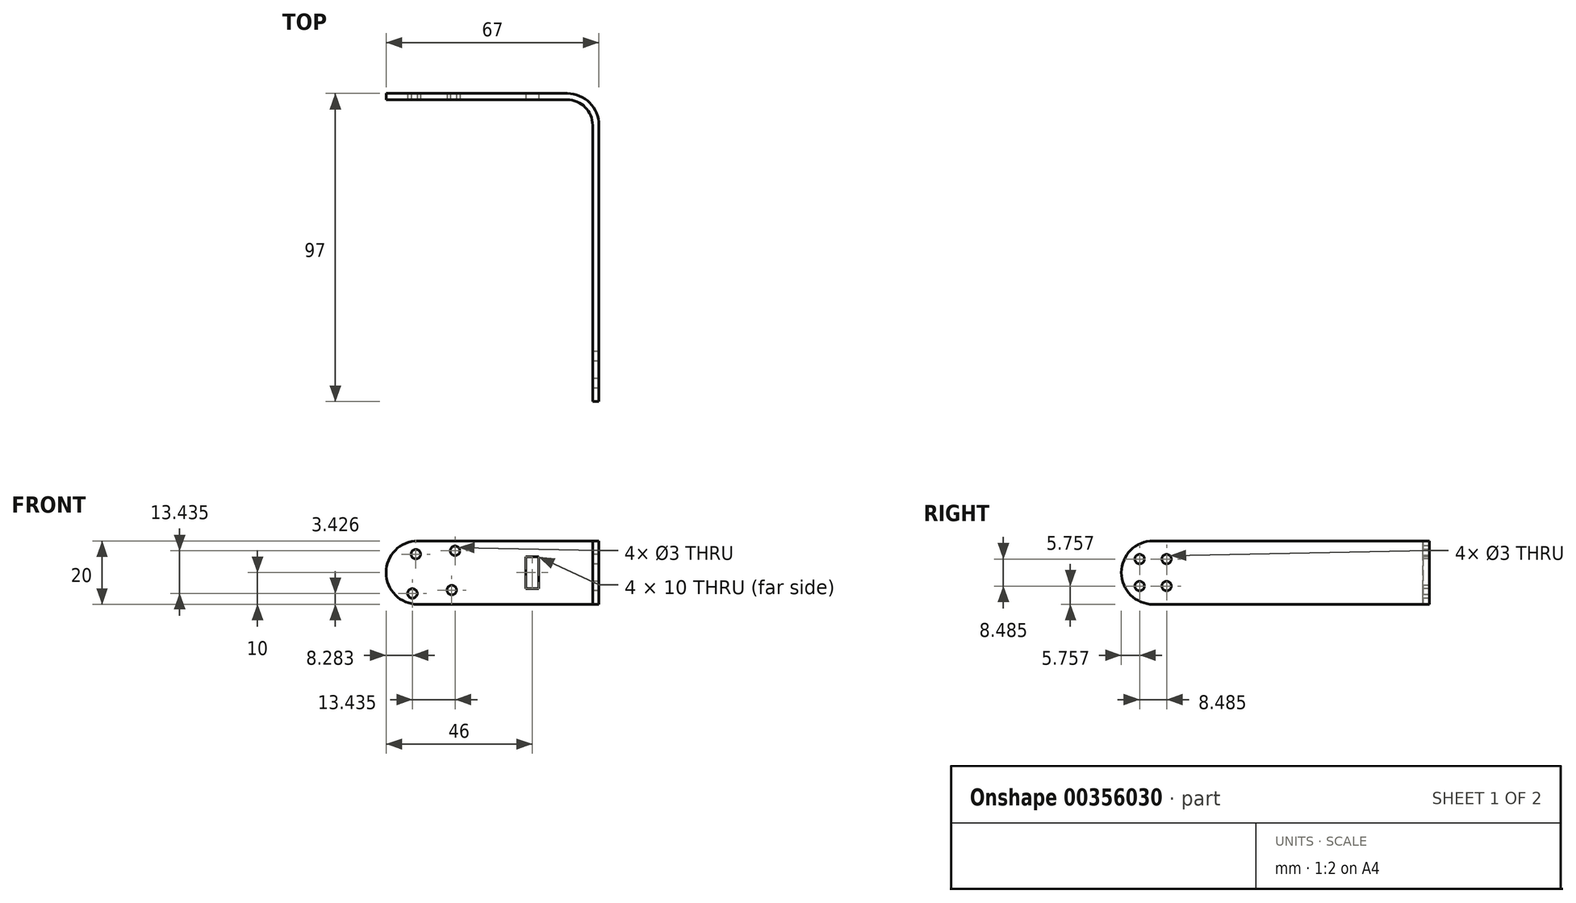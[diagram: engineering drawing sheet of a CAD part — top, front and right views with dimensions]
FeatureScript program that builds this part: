
annotation { "Feature Type Name" : "Feature", "Feature Type Description" : "" }
export const myFeature = defineFeature(function(context is Context, id is Id, definition is map)
    precondition{}
    {
        {
            var Q0;
            Q0=qCreatedBy(makeId("Top.planeOp"),FACE);
            var sketch = newSketch(context, id + "F0", { "sketchPlane" : qUnion([Q0])});
            skLineSegment(sketch, "E0", {"start": v(0, 0) * mm, "end": v(57, 0) * mm});
            skLineSegment(sketch, "E1", {"start": v(65, -8) * mm, "end": v(65, -95) * mm});
            skLineSegment(sketch, "E2.0", {"start": v(67, -8) * mm, "end": v(67, -95) * mm});
            skLineSegment(sketch, "E2.1", {"start": v(0, 2) * mm, "end": v(57, 2) * mm});
            skLineSegment(sketch, "E3", {"start": v(0, 2) * mm, "end": v(0, 0) * mm});
            skLineSegment(sketch, "E4", {"start": v(65, -95) * mm, "end": v(67, -95) * mm});
            skPoint(sketch, "E5.visualSharp", {"position": v(65, 0) * mm});
            skArc(sketch, "E5.filletArc", {"start": v(65, -8) * mm, "mid": v(62.66, -2.34) * mm, "end": v(57, 0) * mm});
            skPoint(sketch, "E6.visualSharp", {"position": v(67, 2) * mm});
            skArc(sketch, "E6.filletArc", {"start": v(67, -8) * mm, "mid": v(64.07, -0.93) * mm, "end": v(57, 2) * mm});
            skSolve(sketch);
        }
        {
            var Q0;
            Q0=qSketchRegion(id+"F0",true);
            extrude(context, id + "F1", {"entities" : qUnion([Q0]), "depth" : 20 * mm});
        }
        {
            var Q0;
            Q0=makeQuery(id+"F1.opExtrude","SWEPT_FACE",FACE,{"disambiguationData":[OSD([sQuery(id+"F0.wireOp",EDGE,"E0")])]});
            var sketch = newSketch(context, id + "F2", { "sketchPlane" : qUnion([Q0])});
            skLineSegment(sketch, "E7", {"start": v(15, 36.62) * mm, "end": v(15, -16.34) * mm});
            skPoint(sketch, "E8", {"position": v(15, 10.14) * mm});
            skLineSegment(sketch, "E9.bottom", {"start": v(44, 15) * mm, "end": v(48, 15) * mm});
            skLineSegment(sketch, "E9.top", {"start": v(44, 5) * mm, "end": v(48, 5) * mm});
            skLineSegment(sketch, "E9.left", {"start": v(44, 15) * mm, "end": v(44, 5) * mm});
            skLineSegment(sketch, "E9.right", {"start": v(48, 15) * mm, "end": v(48, 5) * mm});
            skPoint(sketch, "E10", {"position": v(44, 10) * mm});
            skPoint(sketch, "E11.3.0", {"position": v(21.72, 16.86) * mm});
            skPoint(sketch, "E11.7.0", {"position": v(8.28, 3.43) * mm});
            skPoint(sketch, "E12", {"position": v(15, 2.14) * mm});
            skPoint(sketch, "E13.1.0", {"position": v(20.66, 4.49) * mm});
            skPoint(sketch, "E13.5.0", {"position": v(9.34, 15.8) * mm});
            skSolve(sketch);
        }
        {
            var Q0;
            Q0=makeQuery(id+"F1.opExtrude","SWEPT_FACE",FACE,{"disambiguationData":[OSD([sQuery(id+"F0.wireOp",EDGE,"E1")])]});
            var sketch = newSketch(context, id + "F3", { "sketchPlane" : qUnion([Q0])});
            skLineSegment(sketch, "E14", {"start": v(75, 20) * mm, "end": v(75, 0) * mm, "construction": true});
            skLineSegment(sketch, "E15", {"start": v(75, 10) * mm, "end": v(95, 10) * mm, "construction": true});
            skLineSegment(sketch, "E16", {"start": v(85, 20) * mm, "end": v(85, 0) * mm, "construction": true});
            skPoint(sketch, "E16.startSnap0", {"position": v(85, 10) * mm});
            skPoint(sketch, "E17.middle", {"position": v(32.8, 10) * mm});
            skPoint(sketch, "E18.1.0", {"position": v(80.76, 14.24) * mm});
            skPoint(sketch, "E18.3.0", {"position": v(80.76, 5.76) * mm});
            skPoint(sketch, "E18.5.0", {"position": v(89.24, 5.76) * mm});
            skPoint(sketch, "E18.7.0", {"position": v(89.24, 14.24) * mm});
            skSolve(sketch);
        }
        {
            var Q0;
            Q0=makeQuery(id+"F1.opExtrude","CAP_EDGE",EDGE,{"disambiguationData":[OSD([sQuery(id+"F0.wireOp",EDGE,"E3")])],"isStart":false});
            var Q1;
            Q1=makeQuery(id+"F1.opExtrude","CAP_EDGE",EDGE,{"disambiguationData":[OSD([sQuery(id+"F0.wireOp",EDGE,"E3")])],"isStart":true});
            var Q2;
            Q2=makeQuery(id+"F1.opExtrude","CAP_EDGE",EDGE,{"disambiguationData":[OSD([sQuery(id+"F0.wireOp",EDGE,"E4")])],"isStart":false});
            var Q3;
            Q3=makeQuery(id+"F1.opExtrude","CAP_EDGE",EDGE,{"disambiguationData":[OSD([sQuery(id+"F0.wireOp",EDGE,"E4")])],"isStart":true});
            fillet(context, id + "F4", {"entities" : qUnion([Q0, Q1, Q2, Q3]), "radius" : 10 * mm, "tangentPropagation" : true, "allowEdgeOverflow" : false});
        }
        {
            var Q0;
            Q0=makeQuery(id+"F1.opExtrude","SWEPT_FACE",FACE,{"disambiguationData":[OSD([sQuery(id+"F0.wireOp",EDGE,"E2.0")])]});
            var sketch = newSketch(context, id + "F5", { "sketchPlane" : qUnion([Q0])});
            skSolve(sketch);
        }
        {
            var Q0;
            Q0=sQuery(id+"F3.wireOp",VERTEX,"E18.1.0");
            var Q1;
            Q1=sQuery(id+"F3.wireOp",VERTEX,"E18.3.0");
            var Q2;
            Q2=sQuery(id+"F3.wireOp",VERTEX,"E18.5.0");
            var Q3;
            Q3=sQuery(id+"F3.wireOp",VERTEX,"E18.7.0");
            var Q4;
            Q4=makeQuery(id+"F1.opExtrude","SWEPT_BODY",BODY,{"disambiguationData":[OSD([sQuery(id+"F0.wireOp",EDGE,"E0"),sQuery(id+"F0.wireOp",EDGE,"E1"),sQuery(id+"F0.wireOp",EDGE,"E2.0"),sQuery(id+"F0.wireOp",EDGE,"E2.1"),sQuery(id+"F0.wireOp",EDGE,"E3"),sQuery(id+"F0.wireOp",EDGE,"E4"),sQuery(id+"F0.wireOp",EDGE,"E5.filletArc"),sQuery(id+"F0.wireOp",EDGE,"E6.filletArc")])]});
            hole(context, id + "F6", {"style" : HoleStyle.SIMPLE, "endStyle" : HoleEndStyle.THROUGH, "holeDiameter" : 3 * mm, "tappedDepth" : 4 * mm, "tapClearance" : 3, "locations" : qUnion([Q0, Q1, Q2, Q3]), "scope" : qUnion([Q4])});
        }
        {
            var Q0;
            Q0=makeQuery(id+"F2.imprint","IMPRINT",FACE,{"disambiguationData":[TD([[makeQuery(id+"F2.imprint","IMPRINT",EDGE,{"derivedFrom":sQuery(id+"F2.wireOp",EDGE,"E9.bottom")}),-1.0]])]});
            extrude(context, id + "F7", {"entities" : qUnion([Q0]), "operationType" : NewBodyOperationType.REMOVE, "oppositeDirection" : true, "depth" : 25 * mm});
        }
        {
            var Q0;
            Q0=sQuery(id+"F2.wireOp",VERTEX,"b906b359-9660-4b3f-a93a-f2cba703337d.5.0");
            var Q1;
            Q1=sQuery(id+"F2.wireOp",VERTEX,"E11.7.0");
            var Q2;
            Q2=sQuery(id+"F2.wireOp",VERTEX,"b906b359-9660-4b3f-a93a-f2cba703337d.1.0");
            var Q3;
            Q3=sQuery(id+"F2.wireOp",VERTEX,"E11.3.0");
            var Q4;
            Q4=sQuery(id+"F2.wireOp",VERTEX,"E13.1.0");
            var Q5;
            Q5=sQuery(id+"F2.wireOp",VERTEX,"E13.5.0");
            var Q6;
            Q6=makeQuery(id+"F1.opExtrude","SWEPT_BODY",BODY,{"disambiguationData":[OSD([sQuery(id+"F0.wireOp",EDGE,"E0"),sQuery(id+"F0.wireOp",EDGE,"E1"),sQuery(id+"F0.wireOp",EDGE,"E2.0"),sQuery(id+"F0.wireOp",EDGE,"E2.1"),sQuery(id+"F0.wireOp",EDGE,"E3"),sQuery(id+"F0.wireOp",EDGE,"E4"),sQuery(id+"F0.wireOp",EDGE,"E5.filletArc"),sQuery(id+"F0.wireOp",EDGE,"E6.filletArc")])]});
            hole(context, id + "F8", {"style" : HoleStyle.SIMPLE, "endStyle" : HoleEndStyle.THROUGH, "holeDiameter" : 3 * mm, "tappedDepth" : 4 * mm, "tapClearance" : 3, "locations" : qUnion([Q0, Q1, Q2, Q3, Q4, Q5]), "scope" : qUnion([Q6])});
        }
    });
